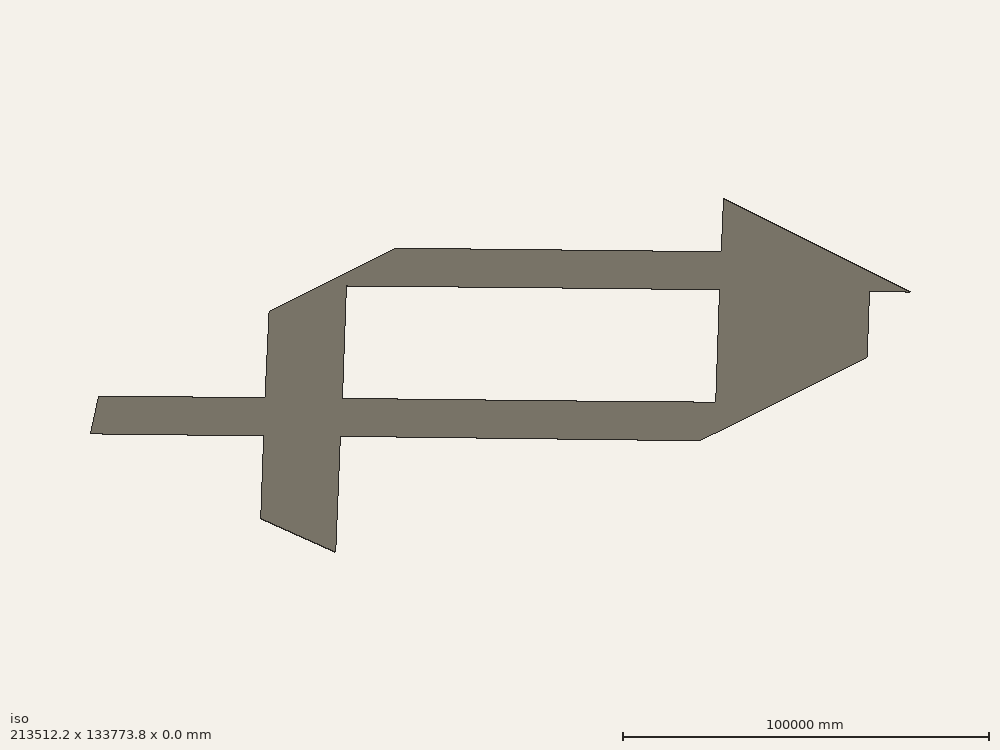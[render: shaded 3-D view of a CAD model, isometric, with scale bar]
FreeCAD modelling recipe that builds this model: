
FCSTD DOCUMENT  (FreeCAD 0.19R18652 (Git))
Label: 15 N_Hancock site
License: All rights reserved
LicenseURL: http://en.wikipedia.org/wiki/All_rights_reserved
objects: Part::Part2DObjectPython×68, App::FeaturePython×51, TechDraw::DrawViewSymbol×9, TechDraw::DrawViewDraft×8, TechDraw::DrawViewClip×5, App::DocumentObjectGroup×5, TechDraw::DrawSVGTemplate×4, TechDraw::DrawPage×4, Image::ImagePlane×1, Part::Cut×1
note: 69 computed .brp shape members not serialized (recipe doc carries the construction recipe); baked Part::Feature solids carry a one-line shape summary decoded from their .brp

FEATURE [Image::ImagePlane] ImagePlane
  XSize = 213448
  YSize = 133615
FEATURE [Part::Part2DObjectPython] Wire  # Draft 2D object (typed FeaturePython)
  Area = 1.04713e+09
  ChamferSize = 0
  Closed = true
  End = (3595.12,13281.7,0)
  FilletRadius = 0
  Length = 171081
  MakeFace = true
  Placement = pos=(-18425.3,-8041.37,0) rot=(0,0,1;0rad)
  Points = (8) [(0,0,0),(16501.4,-17298.5,0),(38495.4,4065.74,0),(31443.5,11545.3,0),(53741.5,33108.7,0),(46730.2,40390.5,0),(24402.7,18854.4,0),(22020.5,21323,0)]
  Start = (-18425.3,-8041.37,0)
  Subdivisions = 0
FEATURE [Part::Part2DObjectPython] Line  # Draft 2D object (typed FeaturePython)
  Area = 0
  ChamferSize = 0
  Closed = false
  End = (-26.9963,-49.3044,0)
  FilletRadius = 0
  Length = 57.0115
  MakeFace = true
  Placement = pos=(-66.3614,-8.06477,0) rot=(0,0,1;0rad)
  Points = (2) [(0,0,0),(39.3651,-41.2396,0)]
  Start = (-66.3614,-8.06477,0)
  Subdivisions = 0
FEATURE [Part::Part2DObjectPython] Wire001  label="Existing building"  # Draft 2D object (typed FeaturePython)
  Area = 4.1645e+08
  ChamferSize = 0
  Closed = true
  End = (802.63,10577.6,0)
  FilletRadius = 0
  Length = 81872.7
  MakeFace = true
  Placement = pos=(15936.7,-5214.36,0) rot=(0,0,1;0rad)
  Points = (4) [(0,0,0),(-13529.7,-13483.2,0),(-28601.5,2751.1,0),(-15134,15792,0)]
  Start = (15936.7,-5214.36,0)
  Subdivisions = 0
FEATURE [Part::Part2DObjectPython] Line001  # Draft 2D object (typed FeaturePython)
  Area = 0
  ChamferSize = 0
  Closed = false
  End = (-33624.1,7891.59,0)
  FilletRadius = 0
  Length = 61543.3
  MakeFace = true
  Placement = pos=(10791.9,50716.9,0) rot=(0,0,1;0rad)
  Points = (2) [(-112.189,-108.171,0),(-44415.9,-42825.3,0)]
  Start = (10679.7,50608.7,0)
  Subdivisions = 0
FEATURE [Part::Part2DObjectPython] Line002  # Draft 2D object (typed FeaturePython)
  Area = 0
  ChamferSize = 0
  Closed = false
  End = (3595.12,13281.7,0)
  FilletRadius = 0
  Length = 21954
  MakeFace = true
  Placement = pos=(3461.65,13054.6,0) rot=(0,0,1;0rad)
  Points = (2) [(-15002.8,16129,0),(133.473,227.049,0)]
  Start = (-11541.2,29183.7,0)
  Subdivisions = 0
FEATURE [Part::Part2DObjectPython] Line003  # Draft 2D object (typed FeaturePython)
  Area = 0
  ChamferSize = 0
  Closed = false
  End = (20070.1,-3975.63,0)
  FilletRadius = 0
  Length = 40805.7
  MakeFace = true
  Placement = pos=(20280.9,-3912.88,0) rot=(0,0,1;0rad)
  Points = (2) [(28041.8,-29505.8,0),(-210.816,-62.7537,0)]
  Start = (48322.6,-33418.7,0)
  Subdivisions = 0
FEATURE [Part::Part2DObjectPython] Line004  # Draft 2D object (typed FeaturePython)
  Area = 0
  ChamferSize = 0
  Closed = false
  End = (12819.8,-11272.6,0)
  FilletRadius = 0
  Length = 40597.7
  MakeFace = true
  Placement = pos=(12819.8,-11272.6,0) rot=(0,0,1;0rad)
  Points = (2) [(28094.1,-29306.8,0),(0,0,0)]
  Start = (40914,-40579.5,0)
  Subdivisions = 0
FEATURE [Part::Part2DObjectPython] Line005  # Draft 2D object (typed FeaturePython)
  Area = 0
  ChamferSize = 0
  Closed = false
  End = (9285.05,-36936.9,0)
  FilletRadius = 0
  Length = 20313.7
  MakeFace = true
  Placement = pos=(8396.39,-37813.2,0) rot=(0,0,1;0rad)
  Points = (2) [(15353.4,15138.7,0),(888.661,876.231,0)]
  Start = (23749.8,-22674.5,0)
  Subdivisions = 0
FEATURE [Part::Part2DObjectPython] Line006  # Draft 2D object (typed FeaturePython)
  Area = 0
  ChamferSize = 0
  Closed = false
  End = (56571.2,2831.99,0)
  FilletRadius = 0
  Length = 31050.5
  MakeFace = true
  Placement = pos=(57938.7,4146.14,0) rot=(0,0,1;0rad)
  Points = (2) [(-23756.1,-22829,0),(-1367.52,-1314.15,0)]
  Start = (34182.6,-18682.9,0)
  Subdivisions = 0
FEATURE [Part::Part2DObjectPython] Line007  # Draft 2D object (typed FeaturePython)
  Area = 0
  ChamferSize = 0
  Closed = false
  End = (49549.2,10177.8,0)
  FilletRadius = 0
  Length = 31069.9
  MakeFace = true
  Placement = pos=(50227.6,10829.7,0) rot=(0,0,1;0rad)
  Points = (2) [(-23080.2,-22180.9,0),(-678.339,-651.909,0)]
  Start = (27147.4,-11351.2,0)
  Subdivisions = 0
FEATURE [Part::Part2DObjectPython] Line008  # Draft 2D object (typed FeaturePython)
  Area = 0
  ChamferSize = 0
  Closed = false
  End = (20070.1,-3975.63,0)
  FilletRadius = 0
  Length = 31090.1
  MakeFace = true
  Placement = pos=(42737.8,18013.5,0) rot=(0,0,1;0rad)
  Points = (2) [(-352.194,-341.65,0),(-22667.8,-21989.1,0)]
  Start = (42385.6,17671.8,0)
  Subdivisions = 0
FEATURE [Part::Part2DObjectPython] Line009  # Draft 2D object (typed FeaturePython)
  Area = 0
  ChamferSize = 0
  Closed = false
  End = (-1096.7,18210.8,0)
  FilletRadius = 0
  Length = 30973.4
  MakeFace = true
  Placement = pos=(21701,40335.4,0) rot=(0,0,1;0rad)
  Points = (2) [(-570.551,-553.704,0),(-22797.7,-22124.6,0)]
  Start = (21130.5,39781.7,0)
  Subdivisions = 0
FEATURE [Part::Part2DObjectPython] Line010  # Draft 2D object (typed FeaturePython)
  Area = 0
  ChamferSize = 0
  Closed = false
  End = (-3426.03,20658,0)
  FilletRadius = 0
  Length = 30663.4
  MakeFace = true
  Placement = pos=(-2908.91,21158.5,0) rot=(0,0,1;0rad)
  Points = (2) [(-22551.3,-21825.2,0),(-517.124,-500.475,0)]
  Start = (-25460.2,-666.694,0)
  Subdivisions = 0
FEATURE [Part::Part2DObjectPython] Line011  # Draft 2D object (typed FeaturePython)
  Area = 0
  ChamferSize = 0
  Closed = false
  End = (-44317.6,19101.7,0)
  FilletRadius = 0
  Length = 37512.1
  MakeFace = true
  Placement = pos=(-18425.3,-8041.37,0) rot=(0,0,1;0rad)
  Points = (2) [(0,0,0),(-25892.3,27143.1,0)]
  Start = (-18425.3,-8041.37,0)
  Subdivisions = 0
FEATURE [Part::Part2DObjectPython] Line012  # Draft 2D object (typed FeaturePython)
  Area = 0
  ChamferSize = 0
  Closed = false
  End = (-103.235,61779.8,0)
  FilletRadius = 0
  Length = 40904.6
  MakeFace = true
  Placement = pos=(28304.8,32349.1,0) rot=(0,0,1;0rad)
  Points = (2) [(0,0,0),(-28408.1,29430.7,0)]
  Start = (28304.8,32349.1,0)
  Subdivisions = 0
FEATURE [Part::Part2DObjectPython] Line013  # Draft 2D object (typed FeaturePython)
  Area = 0
  ChamferSize = 0
  Closed = false
  End = (70621.3,-11866.1,0)
  FilletRadius = 0
  Length = 51093.3
  MakeFace = true
  Placement = pos=(35316.2,25067.3,0) rot=(0,0,1;0rad)
  Points = (2) [(0,0,0),(35305.1,-36933.5,0)]
  Start = (35316.2,25067.3,0)
  Subdivisions = 0
FEATURE [Part::Part2DObjectPython] Line014  # Draft 2D object (typed FeaturePython)
  Area = 0
  ChamferSize = 0
  Closed = false
  End = (26381.8,-54625.5,0)
  FilletRadius = 0
  Length = 40729.1
  MakeFace = true
  Placement = pos=(-1923.97,-25339.9,0) rot=(0,0,1;0rad)
  Points = (2) [(0,0,0),(28305.7,-29285.6,0)]
  Start = (-1923.97,-25339.9,0)
  Subdivisions = 0
FEATURE [Part::Part2DObjectPython] Line015  # Draft 2D object (typed FeaturePython)
  Area = 0
  ChamferSize = 0
  Closed = false
  End = (-44357.7,19063.1,0)
  FilletRadius = 0
  Length = 61507.5
  MakeFace = true
  Points = (2) [(-103.235,61779.8,0),(-44357.7,19063.1,0)]
  Start = (-103.235,61779.8,0)
  Subdivisions = 0
FEATURE [Part::Part2DObjectPython] Line016  # Draft 2D object (typed FeaturePython)
  Area = 0
  ChamferSize = 0
  Closed = false
  End = (26161.4,-54838.4,0)
  FilletRadius = 0
  Length = 61832.9
  MakeFace = true
  Points = (2) [(70621.3,-11866.1,0),(26161.4,-54838.4,0)]
  Start = (70621.3,-11866.1,0)
  Subdivisions = 0
FEATURE [Part::Part2DObjectPython] Wire002  # Draft 2D object (typed FeaturePython)
  Area = 0
  ChamferSize = 0
  Closed = false
  End = (8487.83,-66587.6,0)
  FilletRadius = 0
  Length = 162046
  MakeFace = true
  Placement = pos=(-105250,-39213.2,0) rot=(0,0,1;0rad)
  Points = (3) [(0,0,0),(45826.8,43996.5,0),(113738,-27374.4,0)]
  Start = (-105250,-39213.2,0)
  Subdivisions = 0
FEATURE [Part::Part2DObjectPython] Wire003  # Draft 2D object (typed FeaturePython)
  Area = 0
  ChamferSize = 0
  Closed = false
  End = (106683,-49683.6,0)
  FilletRadius = 0
  Length = 47347.4
  MakeFace = true
  Placement = pos=(72905.8,-66693,0) rot=(0,0,1;0rad)
  Points = (3) [(0,0,0),(25990.9,25090.7,0),(33776.8,17009.5,0)]
  Start = (72905.8,-66693,0)
  Subdivisions = 0
FEATURE [Part::Part2DObjectPython] Wire004  # Draft 2D object (typed FeaturePython)
  Area = 0
  ChamferSize = 0
  Closed = false
  End = (24054.2,66877.6,0)
  FilletRadius = 0
  Length = 118181
  MakeFace = true
  Placement = pos=(106665,22619.6,0) rot=(0,0,1;0rad)
  Points = (3) [(0,0,0),(-21005.7,-20112.4,0),(-82610.7,44257.9,0)]
  Start = (106665,22619.6,0)
  Subdivisions = 0
FEATURE [Part::Part2DObjectPython] Wire005  # Draft 2D object (typed FeaturePython)
  Area = 0
  ChamferSize = 0
  Closed = false
  End = (-90645.7,67080.7,0)
  FilletRadius = 0
  Length = 92567.1
  MakeFace = true
  Placement = pos=(-25016.6,66790,0) rot=(0,0,1;0rad)
  Points = (3) [(0,0,0),(-34041.5,-32480.4,0),(-65629,290.656,0)]
  Start = (-25016.6,66790,0)
  Subdivisions = 0
FEATURE [Part::Part2DObjectPython] Wire006  # Draft 2D object (typed FeaturePython)
  Area = 0
  ChamferSize = 0
  Closed = false
  End = (-106729,-11681.7,0)
  FilletRadius = 0
  Length = 92713.7
  MakeFace = true
  Placement = pos=(-106830,54078,0) rot=(0,0,1;0rad)
  Points = (3) [(0,0,0),(32714.7,-34282.2,0),(100.719,-65759.8,0)]
  Start = (-106830,54078,0)
  Subdivisions = 0
FEATURE [App::FeaturePython] Text  # WARN: FeaturePython — macro-defined, semantics opaque (R4)
  Placement = pos=(-45416.2,17806.4,0) rot=(0,0,-1;0.808978rad)
  Text = N HANCOCK ST
FEATURE [App::FeaturePython] Text001  # WARN: FeaturePython — macro-defined, semantics opaque (R4)
  Placement = pos=(-44903.8,19464,0) rot=(0,0,1;0.767719rad)
  Text = E MIFFLIN ST
FEATURE [App::FeaturePython] Text002  # WARN: FeaturePython — macro-defined, semantics opaque (R4)
  Placement = pos=(65660.9,-5269.52,0) rot=(0,0,-1;0.805821rad)
  Text = N FRANKLIN ST
FEATURE [App::FeaturePython] Text003  # WARN: FeaturePython — macro-defined, semantics opaque (R4)
  Placement = pos=(63903.1,-20917.1,0) rot=(0,0,1;0.768386rad)
  Text = E WASHINGTON AVE
FEATURE [Part::Part2DObjectPython] Line018  # Draft 2D object (typed FeaturePython)
  Area = 0
  ChamferSize = 0
  Closed = false
  End = (25014.2,29175,0)
  FilletRadius = 0
  Length = 10114.5
  MakeFace = true
  Points = (2) [(32029.6,21889,0),(25014.2,29175,0)]
  Start = (32029.6,21889,0)
  Subdivisions = 0
FEATURE [Part::Part2DObjectPython] Line022  # Draft 2D object (typed FeaturePython)
  Area = 0
  ChamferSize = 0
  Closed = false
  End = (1384.25,-22184.1,0)
  FilletRadius = 0
  Length = 23906.8
  MakeFace = true
  Points = (2) [(-15117.1,-4885.6,0),(1384.25,-22184.1,0)]
  Start = (-15117.1,-4885.6,0)
  Subdivisions = 0
FEATURE [App::FeaturePython] Dimension  # Draft dimension (typed FeaturePython)
  Diameter = false
  Dimline = (-1177.23,12550.3,0)
  Direction = (0,0,0)
  Distance = 30652.4
  End = (3595.12,13281.7,0)
  Normal = (0,0,1)
  Start = (-18425.3,-8041.37,0)
FEATURE [App::FeaturePython] Dimension001  # Draft dimension (typed FeaturePython)
  Diameter = false
  Dimline = (-7526.87,-23407.2,0)
  Direction = (0,0,0)
  Distance = 23906.8
  End = (-1923.97,-25339.9,0)
  Normal = (0,0,1)
  Start = (-18425.3,-8041.37,0)
FEATURE [App::FeaturePython] Dimension002  # Draft dimension (typed FeaturePython)
  Diameter = false
  Dimline = (19021.1,-8668.65,0)
  Direction = (0,0,0)
  Distance = 30662.2
  End = (20070.1,-3975.63,0)
  Normal = (0,0,1)
  Start = (-1923.97,-25339.9,0)
FEATURE [App::FeaturePython] Dimension003  # Draft dimension (typed FeaturePython)
  Diameter = false
  Dimline = (23033.4,28711.1,0)
  Direction = (0,0,0)
  Distance = 31021.3
  End = (28304.8,32349.1,0)
  Normal = (0,0,1)
  Start = (5977.33,10813,0)
FEATURE [App::FeaturePython] Dimension004  # Draft dimension (typed FeaturePython)
  Diameter = false
  Dimline = (36237.5,20611.2,0)
  Direction = (0,0,0)
  Distance = 31019
  End = (35316.2,25067.3,0)
  Normal = (0,0,1)
  Start = (13018.2,3503.93,0)
FEATURE [App::FeaturePython] Dimension005  # Draft dimension (typed FeaturePython)
  Diameter = false
  Dimline = (34894.1,26811.8,0)
  Direction = (0,0,0)
  Distance = 10108.5
  End = (35316.2,25067.3,0)
  Normal = (0,0,1)
  Start = (28304.8,32349.1,0)
FEATURE [App::FeaturePython] Dimension006  # Draft dimension (typed FeaturePython)
  Diameter = false
  Dimline = (-684.958,-23208.5,0)
  Direction = (0,0,0)
  Distance = 4572.19
  End = (1355.67,-22154.2,0)
  Normal = (0,0,1)
  Start = (-1923.97,-25339.9,0)
FEATURE [App::FeaturePython] Dimension007  # Draft dimension (typed FeaturePython)
  Diameter = false
  Dimline = (34178.3,24674.7,0)
  Direction = (0,0,0)
  Distance = 4572
  End = (35316.2,25067.3,0)
  Normal = (0,0,1)
  Start = (32022.7,21896.2,0)
FEATURE [Part::Part2DObjectPython] Line024  # Draft 2D object (typed FeaturePython)
  Area = 0
  ChamferSize = 0
  Closed = false
  End = (7804.54,5528.17,0)
  FilletRadius = 0
  Length = 40485.3
  MakeFace = true
  Placement = pos=(9504.84,7165.33,0) rot=(0,0,1;0rad)
  Points = (2) [(27463.5,26443.6,0),(-1700.31,-1637.16,0)]
  Start = (36968.4,33608.9,0)
  Subdivisions = 0
FEATURE [Part::Part2DObjectPython] Rectangle  # Draft 2D object (typed FeaturePython)
  Area = 1.50503e+07
  ChamferSize = 0
  Columns = 1
  FilletRadius = 0
  Height = 2743.2
  Length = 5486.4
  MakeFace = true
  Placement = pos=(22172.4,23739,0) rot=(0,0,-1;0.018041rad)
  Rows = 1
FEATURE [Part::Part2DObjectPython] Rectangle001  label="Rectangle"  # Draft 2D object (typed FeaturePython)
  Area = 1.50503e+07
  ChamferSize = 0
  Columns = 1
  FilletRadius = 0
  Height = 2743.2
  Length = 5486.4
  MakeFace = true
  Placement = pos=(19380.2,21045.8,0) rot=(0,0,-1;0.018041rad)
  Rows = 1
FEATURE [Part::Part2DObjectPython] Rectangle002  label="Rectangle"  # Draft 2D object (typed FeaturePython)
  Area = 1.50503e+07
  ChamferSize = 0
  Columns = 1
  FilletRadius = 0
  Height = 2743.2
  Length = 5486.4
  MakeFace = true
  Placement = pos=(16587.9,18352.5,0) rot=(0,0,-1;0.018041rad)
  Rows = 1
FEATURE [Part::Part2DObjectPython] Rectangle003  label="Rectangle"  # Draft 2D object (typed FeaturePython)
  Area = 1.50503e+07
  ChamferSize = 0
  Columns = 1
  FilletRadius = 0
  Height = 2743.2
  Length = 5486.4
  MakeFace = true
  Placement = pos=(11003.5,12966,0) rot=(0,0,-1;0.018041rad)
  Rows = 1
FEATURE [Part::Part2DObjectPython] Rectangle004  label="Rectangle"  # Draft 2D object (typed FeaturePython)
  Area = 1.50503e+07
  ChamferSize = 0
  Columns = 1
  FilletRadius = 0
  Height = 2743.2
  Length = 5486.4
  MakeFace = true
  Placement = pos=(13795.7,15659.2,0) rot=(0,0,-1;0.018041rad)
  Rows = 1
FEATURE [Part::Part2DObjectPython] Rectangle005  label="Rectangle"  # Draft 2D object (typed FeaturePython)
  Area = 1.50503e+07
  ChamferSize = 0
  Columns = 1
  FilletRadius = 0
  Height = 2743.2
  Length = 5486.4
  MakeFace = true
  Placement = pos=(8211.22,10272.7,0) rot=(0,0,-1;0.018041rad)
  Rows = 1
FEATURE [Part::Part2DObjectPython] Rectangle007  label="Rectangle"  # Draft 2D object (typed FeaturePython)
  Area = 1.50503e+07
  ChamferSize = 0
  Columns = 1
  FilletRadius = 0
  Height = 2743.2
  Length = 5486.4
  MakeFace = true
  Placement = pos=(23038.1,27272.4,0) rot=(0,0,-1;0.804317rad)
  Rows = 1
FEATURE [App::FeaturePython] Text004  # WARN: FeaturePython — macro-defined, semantics opaque (R4)
  Placement = pos=(-16015.3,-6054.01,0) rot=(0,0,-1;0.808978rad)
  Text = SETBACK
FEATURE [App::FeaturePython] Text005  # WARN: FeaturePython — macro-defined, semantics opaque (R4)
  Placement = pos=(25183.8,29191.7,0) rot=(0,0,-1;0.808978rad)
  Text = SETBACK
FEATURE [App::FeaturePython] Text006  # WARN: FeaturePython — macro-defined, semantics opaque (R4)
  Placement = pos=(36344.8,32541.2,0) rot=(0,0,-1;0.807936rad)
  Text = ONLY 50% OF THE FRONTAGE | CAN BE OCCUPIED BY | PARKING
FEATURE [App::FeaturePython] Dimension009  # Draft dimension (typed FeaturePython)
  Diameter = false
  Dimline = (27213.5,18597.6,0)
  Direction = (0,0,0)
  Distance = 4302.77
  End = (27856.8,17853.7,0)
  Normal = (0,0,1)
  Start = (24865.7,20946.8,0)
FEATURE [Part::Part2DObjectPython] Line025  # Draft 2D object (typed FeaturePython)
  Area = 0
  ChamferSize = 0
  Closed = false
  End = (21204.7,17415.6,0)
  FilletRadius = 0
  Length = 7995.18
  MakeFace = true
  Placement = pos=(27657.9,23640,0) rot=(0,0,1;0rad)
  Points = (2) [(-698.692,-673.925,0),(-6453.21,-6224.46,0)]
  Start = (26959.2,22966.1,0)
  Subdivisions = 0
FEATURE [App::FeaturePython] Dimension008  # Draft dimension (typed FeaturePython)
  Diameter = false
  Dimline = (28275.6,26130.3,0)
  Direction = (0,0,0)
  Distance = 5097.53
  End = (28549.8,25503,0)
  Normal = (0,0,1)
  Start = (25014.2,29175,0)
FEATURE [Part::Part2DObjectPython] Circle  # Draft 2D object (typed FeaturePython)
  Area = 1.11035e+07
  FirstAngle = 0
  LastAngle = 0
  MakeFace = true
  Placement = pos=(-45678.7,-16653.5,0) rot=(0,0,1;0rad)
  Radius = 1879.98
FEATURE [Part::Part2DObjectPython] Line027  # Draft 2D object (typed FeaturePython)
  Area = 0
  ChamferSize = 0
  Closed = false
  End = (-45678.7,-18533.5,0)
  FilletRadius = 0
  Length = 3759.97
  MakeFace = true
  Placement = pos=(-45678.7,-14773.5,0) rot=(0,0,1;0rad)
  Points = (2) [(0,0,0),(0,-3759.97,0)]
  Start = (-45678.7,-14773.5,0)
  Subdivisions = 0
FEATURE [Part::Part2DObjectPython] Wire007  # Draft 2D object (typed FeaturePython)
  Area = 3.53434e+06
  ChamferSize = 0
  Closed = true
  End = (-43798.7,-16653.5,0)
  FilletRadius = 0
  Length = 9077.37
  MakeFace = true
  Placement = pos=(-47558.7,-16653.5,0) rot=(0,0,1;0rad)
  Points = (3) [(0,0,0),(1879.98,1879.98,0),(3759.97,0,0)]
  Start = (-47558.7,-16653.5,0)
  Subdivisions = 0
FEATURE [Part::Part2DObjectPython] Wire008  label="Sta norte"  # Draft 2D object (typed FeaturePython)
  Area = 1.76717e+06
  ChamferSize = 0
  Closed = true
  End = (-45678.7,-16653.5,0)
  FilletRadius = 0
  Length = 6418.67
  MakeFace = true
  Placement = pos=(-47558.7,-16653.5,0) rot=(0,0,1;0rad)
  Points = (3) [(0,0,0),(1879.98,1879.98,0),(1879.98,0,0)]
  Start = (-47558.7,-16653.5,0)
  Subdivisions = 0
FEATURE [App::FeaturePython] Text007  # WARN: FeaturePython — macro-defined, semantics opaque (R4)
  Placement = pos=(-2690.19,-1131.57,0) rot=(0,0,-1;0.808978rad)
  Text = EXISTING BUILDING
FEATURE [App::FeaturePython] Text008  # WARN: FeaturePython — macro-defined, semantics opaque (R4)
  Placement = pos=(19057.9,12203.9,0) rot=(0,0,1;0.763757rad)
  Text = 6 x 9x18 STALLS
FEATURE [Part::Part2DObjectPython] Wire009  # Draft 2D object (typed FeaturePython)
  Area = 6.39951e+08
  ChamferSize = 0
  Closed = true
  End = (-1923.97,-25339.9,0)
  FilletRadius = 0
  Length = 101357
  MakeFace = true
  Placement = pos=(-18425.3,-8041.37,0) rot=(0,0,1;0rad)
  Points = (5) [(0,0,0),(19228,18619,0),(34362,2827,0),(35739.9,1389.18,0),(16501.4,-17298.5,0)]
  Start = (-18425.3,-8041.37,0)
  Subdivisions = 0
FEATURE [Part::Part2DObjectPython] Wire010  label="Blue cotour"  # Draft 2D object (typed FeaturePython)
  Area = 2.09786e+08
  ChamferSize = 0
  Closed = true
  End = (24964.7,26432.3,0)
  FilletRadius = 0
  Length = 78881.9
  MakeFace = true
  Placement = pos=(27702.6,26382.9,0) rot=(0,0,1;0rad)
  Points = (24) [(0,0,0),(1728.63,-31.1927,0),(4134.48,2285.31,0),(6554.12,-220.027,0),(3269.91,-3396.04,0),(4326.97,-4493.86,0),(-7977.16,-16317.9,0),+17 more]
  Start = (27702.6,26382.9,0)
  Subdivisions = 0
FEATURE [Part::Part2DObjectPython] Wire011  # Draft 2D object (typed FeaturePython)
  Area = 1.87779e+08
  ChamferSize = 0
  Closed = true
  End = (-1923.97,-25339.9,0)
  FilletRadius = 0
  Length = 63520
  MakeFace = true
  Placement = pos=(-18425.3,-8041.37,0) rot=(1,0,0;3.14159rad)
  Points = (4) [(0,0,0),(5760.55,-5578.1,0),(22021.1,11936.8,0),(16501.4,17298.5,0)]
  Start = (-18425.3,-8041.37,0)
  Subdivisions = 0
FEATURE [Part::Part2DObjectPython] Wire012  # Draft 2D object (typed FeaturePython)
  Area = 1.7888e+10
  ChamferSize = 0
  Closed = true
  End = (-74114.9,19795.9,0)
  FilletRadius = 0
  Length = 746954
  MakeFace = true
  Placement = pos=(-106830,54078,0) rot=(0,0,1;0rad)
  Points = (15) [(0,0,0),(16183.9,13002.7,0),(47762.3,-19758.9,0),(81812.9,12712,0),(130884,12799.5,0),(192489,-51570.8,0),(213495,-31458.4,0),(213512,-103762,0),+7 more]
  Start = (-106830,54078,0)
  Subdivisions = 0
FEATURE [Part::Part2DObjectPython] Wire013  # Draft 2D object (typed FeaturePython)
  Area = 6.29559e+09
  ChamferSize = 0
  Closed = true
  End = (-1923.97,-25339.9,0)
  FilletRadius = 0
  Length = 327288
  MakeFace = true
  Placement = pos=(-44357.7,19063.1,0) rot=(0,0,1;0rad)
  Points = (6) [(0,0,0),(44254.4,42716.7,0),(79673.8,6004.29,0),(114979,-30929.2,0),(70739.4,-73688.5,0),(42433.7,-44402.9,0)]
  Start = (-44357.7,19063.1,0)
  Subdivisions = 0
FEATURE [Part::Cut] Cut
  Base = -> Wire012
  Tool = -> Wire013
FEATURE [TechDraw::DrawSVGTemplate] Template
  EditableTexts = ADDRESS=15N HANCOCK ST, MADISON WI; DATE=Date; DESCRIPTION=Description; PROJECT NAME=STUDY FOR A BACKLOT
  Height = 279.4
  Orientation = 1
  Width = 431.8
FEATURE [TechDraw::DrawViewSymbol] Symbol
  EditableTexts = 01 | PLAN VIEW OF PARCEL | 1/32 = 1-0
  LockPosition = false
  Rotation = 0
  ScaleType = 2
  Symbol = <blob: 4965 chars omitted>
  X = 87.9124
  Y = 44.9176
FEATURE [TechDraw::DrawViewSymbol] Symbol001
  LockPosition = false
  Rotation = 0
  Scale = 0.35
  ScaleType = 2
  Symbol = <blob: 2355908 chars omitted>
  X = -0.52207
  Y = 0.671524
FEATURE [TechDraw::DrawViewClip] Clip001
  Height = 60.96
  LockPosition = false
  Rotation = 0
  ScaleType = 0
  ShowFrame = false
  Views = -> [Symbol001]
  Width = 60.96
  X = 60.1906
  Y = 100.238
FEATURE [App::DocumentObjectGroup] Group001  label="Existing"
  Group = -> [Wire001,Wire011,Cut,Wire,Line,Line001,Line002,Line003,Line004,Line005,Line006,Line007,Line008,Line009,Line010,Line011,Line012,Line013,Line014,Line015,Line016,Wire002,Wire003,Wire004,Wire006,Wire005,Line022,Line018,Wire009,Wire008,Wire007,Line027,Circle,Text007,Text005,Dimension007,Dimension005,Dimension006,Dimension004,Dimension003,Dimension002,Dimension001,Dimension,Text003,Text002,Text001,Text]
FEATURE [TechDraw::DrawViewDraft] DraftView
  Direction = (0,0,1)
  FontSize = 5.5
  LineSpacing = 5
  LineStyle = Solid
  LineWidth = 0.15
  LockPosition = false
  OverrideStyle = false
  Rotation = 0
  Scale = 0.00260417
  ScaleType = 2
  Source = -> Group001
  Symbol = <blob: 16925 chars omitted>
  X = 0
  Y = 0
FEATURE [App::DocumentObjectGroup] Group002  label="Parking only"
  Group = -> [Wire010,Line024,Rectangle,Rectangle001,Rectangle002,Rectangle003,Rectangle004,Rectangle005,Rectangle007,Line025,Dimension008,Text004,Text006,Dimension009,Text008]
FEATURE [Part::Part2DObjectPython] Line029  # Draft 2D object (typed FeaturePython)
  Area = 0
  ChamferSize = 0
  Closed = false
  End = (25711.8,28450.5,0)
  FilletRadius = 0
  Length = 20353.1
  MakeFace = true
  Points = (2) [(11062.7,14320.7,0),(25711.8,28450.5,0)]
  Start = (11062.7,14320.7,0)
  Subdivisions = 0
FEATURE [Part::Part2DObjectPython] Line032  # Draft 2D object (typed FeaturePython)
  Area = 0
  ChamferSize = 0
  Closed = false
  End = (35316.2,25067.3,0)
  FilletRadius = 0
  Length = 31019
  MakeFace = true
  Placement = pos=(13018.2,3503.93,0) rot=(0,0,1;0rad)
  Points = (2) [(0,0,0),(22298,21563.4,0)]
  Start = (13018.2,3503.93,0)
  Subdivisions = 0
FEATURE [Part::Part2DObjectPython] Line033  # Draft 2D object (typed FeaturePython)
  Area = 0
  ChamferSize = 0
  Closed = false
  End = (31331.9,22613.6,0)
  FilletRadius = 0
  Length = 20351.2
  MakeFace = true
  Points = (2) [(16702.5,8466.08,0),(31331.9,22613.6,0)]
  Start = (16702.5,8466.08,0)
  Subdivisions = 0
FEATURE [Part::Part2DObjectPython] Line036  # Draft 2D object (typed FeaturePython)
  Area = 0
  ChamferSize = 0
  Closed = false
  End = (13018.2,3503.93,0)
  FilletRadius = 0
  Length = 10148.7
  MakeFace = true
  Placement = pos=(5977.33,10813,0) rot=(0,0,1;0rad)
  Points = (2) [(0,0,0),(7040.85,-7309.08,0)]
  Start = (5977.33,10813,0)
  Subdivisions = 0
FEATURE [App::FeaturePython] Dimension010  # Draft dimension (typed FeaturePython)
  Diameter = false
  Dimline = (23300,27000,0)
  Direction = (0,0,0)
  Distance = 1005.84
  End = (25711.8,28450.5,0)
  Normal = (0,0,1)
  Start = (25014.2,29175,0)
FEATURE [App::FeaturePython] Dimension011  # Draft dimension (typed FeaturePython)
  Diameter = false
  Dimline = (23735.6,26547.6,0)
  Direction = (0,0,0)
  Distance = 1005.84
  End = (32031.2,21890.5,0)
  Normal = (0,0,1)
  Start = (31331.9,22613.6,0)
FEATURE [Part::Part2DObjectPython] Line037  # Draft 2D object (typed FeaturePython)
  Area = 0
  ChamferSize = 0
  Closed = false
  End = (17408.5,7733.14,0)
  FilletRadius = 0
  Length = 10148.7
  MakeFace = true
  Points = (2) [(10367.7,15042.2,0),(17408.5,7733.14,0)]
  Start = (10367.7,15042.2,0)
  Subdivisions = 0
FEATURE [App::FeaturePython] Dimension012  # Draft dimension (typed FeaturePython)
  Diameter = false
  Dimline = (17400.3,7741.68,0)
  Direction = (0,0,0)
  Distance = 6096.01
  End = (17400.3,7741.68,0)
  Normal = (0,0,1)
  Start = (13018.2,3503.93,0)
FEATURE [App::FeaturePython] Text010  # WARN: FeaturePython — macro-defined, semantics opaque (R4)
  Placement = pos=(7530.44,6471.84,0) rot=(0,0,-1;0.801487rad)
  Text = OPEN SPACE
FEATURE [App::FeaturePython] Text011  # WARN: FeaturePython — macro-defined, semantics opaque (R4)
  Placement = pos=(9130.44,11571.8,0) rot=(0,0,-1;0.801487rad)
  Text = OPEN SPACE
FEATURE [App::FeaturePython] Dimension013  # Draft dimension (typed FeaturePython)
  Diameter = false
  Dimline = (20070.1,-3975.63,0)
  Direction = (0,0,0)
  Distance = 3841.42
  End = (20070.1,-3975.63,0)
  Normal = (0,0,1)
  Start = (17314.6,-6652.19,0)
FEATURE [Part::Part2DObjectPython] Line038  # Draft 2D object (typed FeaturePython)
  Area = 0
  ChamferSize = 0
  Closed = false
  End = (28077.4,18083.6,0)
  FilletRadius = 0
  Length = 8217.7
  MakeFace = true
  Points = (2) [(22377.6,24003.3,0),(28077.4,18083.6,0)]
  Start = (22377.6,24003.3,0)
  Subdivisions = 0
FEATURE [Part::Part2DObjectPython] Line042  # Draft 2D object (typed FeaturePython)
  Area = 0
  ChamferSize = 0
  Closed = false
  End = (26183,20051.1,0)
  FilletRadius = 0
  Length = 5486.41
  MakeFace = true
  Points = (2) [(30126.9,23865.1,0),(26183,20051.1,0)]
  Start = (30126.9,23865.1,0)
  Subdivisions = 0
FEATURE [Part::Part2DObjectPython] Line043  # Draft 2D object (typed FeaturePython)
  Area = 0
  ChamferSize = 0
  Closed = false
  End = (24280.3,22027.2,0)
  FilletRadius = 0
  Length = 5486.41
  MakeFace = true
  Points = (2) [(28224.2,25841.2,0),(24280.3,22027.2,0)]
  Start = (28224.2,25841.2,0)
  Subdivisions = 0
FEATURE [Part::Part2DObjectPython] Line044  # Draft 2D object (typed FeaturePython)
  Area = 0
  ChamferSize = 0
  Closed = false
  End = (26321.5,27817.3,0)
  FilletRadius = 0
  Length = 5486.41
  MakeFace = true
  Points = (2) [(22377.6,24003.3,0),(26321.5,27817.3,0)]
  Start = (22377.6,24003.3,0)
  Subdivisions = 0
FEATURE [Part::Part2DObjectPython] Line045  # Draft 2D object (typed FeaturePython)
  Area = 0
  ChamferSize = 0
  Closed = false
  End = (32029.6,21889,0)
  FilletRadius = 0
  Length = 8229.62
  MakeFace = true
  Placement = pos=(26321.5,27817.3,0) rot=(0,0,1;0rad)
  Points = (2) [(0,0,0),(5708.09,-5928.26,0)]
  Start = (26321.5,27817.3,0)
  Subdivisions = 0
FEATURE [Part::Part2DObjectPython] Wire014  label="Building contour"  # Draft 2D object (typed FeaturePython)
  Area = 1.20638e+08
  ChamferSize = 0
  Closed = true
  End = (21763,24641.6,0)
  FilletRadius = 0
  Length = 45954.7
  MakeFace = true
  Placement = pos=(11062.7,14320.7,0) rot=(0,0,1;0rad)
  Points = (4) [(0,0,0),(5651.09,-5843.6,0),(16325.3,4478.95,0),(10700.3,10321,0)]
  Start = (11062.7,14320.7,0)
  Subdivisions = 0
FEATURE [App::FeaturePython] Text012  # WARN: FeaturePython — macro-defined, semantics opaque (R4)
  Placement = pos=(16915.7,18408.6,0) rot=(0,0,-1;0rad)
  Text = NEW | BUILDING | 1300.70 SQFT
FEATURE [App::FeaturePython] Dimension014  # Draft dimension (typed FeaturePython)
  Diameter = false
  Dimline = (16000,9600,0)
  Direction = (0,0,0)
  Distance = 8129.12
  End = (16713.8,8477.07,0)
  Normal = (0,0,1)
  Start = (11062.7,14320.7,0)
FEATURE [App::FeaturePython] Dimension015  # Draft dimension (typed FeaturePython)
  Diameter = false
  Dimline = (26800,18600,0)
  Direction = (0,0,0)
  Distance = 14864.8
  End = (27388,18799.6,0)
  Normal = (0,0,1)
  Start = (16702.5,8466.08,0)
FEATURE [App::FeaturePython] Text013  # WARN: FeaturePython — macro-defined, semantics opaque (R4)
  Placement = pos=(26502.5,23589.1,0) rot=(0,0,-1;0.000587rad)
  Text = 3 x 9x18' | STALLS
FEATURE [TechDraw::DrawViewDraft] DraftView001
  Direction = (0,0,1)
  FontSize = 5.5
  LineSpacing = 5
  LineStyle = Solid
  LineWidth = 0.15
  LockPosition = false
  OverrideStyle = false
  Rotation = 0
  Scale = 0.00260417
  ScaleType = 2
  Source = -> Group002
  Symbol = <blob: 7460 chars omitted>
  X = 274.42
  Y = 206.151
FEATURE [TechDraw::DrawViewClip] Clip002
  Height = 213.36
  LockPosition = false
  Rotation = 0
  ScaleType = 0
  ShowFrame = false
  Views = -> [DraftView]
  Width = 396.24
  X = 215.9
  Y = 155.7
FEATURE [TechDraw::DrawSVGTemplate] Template001
  EditableTexts = ADDRESS=15N HANCOCK ST, MADISON WI; PROJECT NAME=STUDY FOR A BACKLOT
  Height = 279.4
  Orientation = 1
  Width = 431.8
FEATURE [TechDraw::DrawViewSymbol] Symbol002
  EditableTexts = 01 | PLAN VIEW OF PARCEL - SPLIT LOT W/ PARKING | 1/32 = 1-0
  LockPosition = false
  Rotation = 0
  ScaleType = 2
  Symbol = <blob: 4988 chars omitted>
  X = 87.9124
  Y = 44.9176
FEATURE [TechDraw::DrawViewDraft] DraftView003
  Direction = (0,0,1)
  FontSize = 5.5
  LineSpacing = 5
  LineStyle = Solid
  LineWidth = 0.15
  LockPosition = false
  OverrideStyle = false
  Rotation = 0
  Scale = 0.00260417
  ScaleType = 2
  Source = -> Group001
  Symbol = <blob: 16925 chars omitted>
  X = -20.9742
  Y = -2.70531
FEATURE [TechDraw::DrawViewClip] Clip
  Height = 213.36
  LockPosition = false
  Rotation = 0
  ScaleType = 0
  ShowFrame = false
  Views = -> [DraftView003]
  Width = 396.24
  X = 215.9
  Y = 155.7
FEATURE [App::FeaturePython] Text014  # WARN: FeaturePython — macro-defined, semantics opaque (R4)
  Placement = pos=(19615.7,20408.6,0) rot=(0,0,-1;0.016745rad)
  Text = NEW | BUILDING | 2714.21 SQFT
FEATURE [Part::Part2DObjectPython] Line046  # Draft 2D object (typed FeaturePython)
  Area = 0
  ChamferSize = 0
  Closed = false
  End = (13018.2,3503.93,0)
  FilletRadius = 0
  Length = 10148.7
  MakeFace = true
  Placement = pos=(5977.33,10813,0) rot=(0,0,1;0rad)
  Points = (2) [(0,0,0),(7040.85,-7309.08,0)]
  Start = (5977.33,10813,0)
  Subdivisions = 0
FEATURE [Part::Part2DObjectPython] Line047  # Draft 2D object (typed FeaturePython)
  Area = 0
  ChamferSize = 0
  Closed = false
  End = (31331.9,22613.6,0)
  FilletRadius = 0
  Length = 20351.2
  MakeFace = true
  Points = (2) [(16702.5,8466.08,0),(31331.9,22613.6,0)]
  Start = (16702.5,8466.08,0)
  Subdivisions = 0
FEATURE [App::FeaturePython] Dimension016  # Draft dimension (typed FeaturePython)
  Diameter = false
  Dimline = (23735.6,26547.6,0)
  Direction = (0,0,0)
  Distance = 1005.84
  End = (32031.2,21890.5,0)
  Normal = (0,0,1)
  Start = (31331.9,22613.6,0)
FEATURE [Part::Part2DObjectPython] Line050  # Draft 2D object (typed FeaturePython)
  Area = 0
  ChamferSize = 0
  Closed = false
  End = (17408.5,7733.14,0)
  FilletRadius = 0
  Length = 10148.7
  MakeFace = true
  Points = (2) [(10367.7,15042.2,0),(17408.5,7733.14,0)]
  Start = (10367.7,15042.2,0)
  Subdivisions = 0
FEATURE [App::FeaturePython] Dimension017  # Draft dimension (typed FeaturePython)
  Diameter = false
  Dimline = (17400.3,7741.68,0)
  Direction = (0,0,0)
  Distance = 6096.01
  End = (17400.3,7741.68,0)
  Normal = (0,0,1)
  Start = (13018.2,3503.93,0)
FEATURE [App::FeaturePython] Text015  # WARN: FeaturePython — macro-defined, semantics opaque (R4)
  Placement = pos=(7130.44,6971.84,0) rot=(0,0,-1;0.801487rad)
  Text = OPEN SPACE
FEATURE [App::FeaturePython] Dimension018  # Draft dimension (typed FeaturePython)
  Diameter = false
  Dimline = (23300,27000,0)
  Direction = (0,0,0)
  Distance = 1005.84
  End = (25711.8,28450.5,0)
  Normal = (0,0,1)
  Start = (25014.2,29175,0)
FEATURE [Part::Part2DObjectPython] Line051  # Draft 2D object (typed FeaturePython)
  Area = 0
  ChamferSize = 0
  Closed = false
  End = (25711.8,28450.5,0)
  FilletRadius = 0
  Length = 20353.1
  MakeFace = true
  Points = (2) [(11062.7,14320.7,0),(25711.8,28450.5,0)]
  Start = (11062.7,14320.7,0)
  Subdivisions = 0
FEATURE [Part::Part2DObjectPython] Line052  # Draft 2D object (typed FeaturePython)
  Area = 0
  ChamferSize = 0
  Closed = false
  End = (35316.2,25067.3,0)
  FilletRadius = 0
  Length = 31019
  MakeFace = true
  Placement = pos=(13018.2,3503.93,0) rot=(0,0,1;0rad)
  Points = (2) [(0,0,0),(22298,21563.4,0)]
  Start = (13018.2,3503.93,0)
  Subdivisions = 0
FEATURE [App::FeaturePython] Text016  # WARN: FeaturePython — macro-defined, semantics opaque (R4)
  Placement = pos=(9130.44,11571.8,0) rot=(0,0,-1;0.801487rad)
  Text = OPEN SPACE
FEATURE [App::FeaturePython] Dimension019  # Draft dimension (typed FeaturePython)
  Diameter = false
  Dimline = (20070.1,-3975.63,0)
  Direction = (0,0,0)
  Distance = 3841.42
  End = (20070.1,-3975.63,0)
  Normal = (0,0,1)
  Start = (17314.6,-6652.19,0)
FEATURE [Part::Part2DObjectPython] Wire015  label="Building Contour"  # Draft 2D object (typed FeaturePython)
  Area = 1.65185e+08
  ChamferSize = 0
  Closed = true
  End = (25711.8,28450.5,0)
  FilletRadius = 0
  Length = 56927.5
  MakeFace = true
  Placement = pos=(11062.7,14320.7,0) rot=(0,0,1;0rad)
  Points = (4) [(0,0,0),(5651.09,-5843.6,0),(20274.1,8287.8,0),(14649.1,14129.8,0)]
  Start = (11062.7,14320.7,0)
  Subdivisions = 0
FEATURE [App::FeaturePython] Dimension020  # Draft dimension (typed FeaturePython)
  Diameter = false
  Dimline = (16000,9600,0)
  Direction = (0,0,0)
  Distance = 8129.12
  End = (16713.8,8477.07,0)
  Normal = (0,0,1)
  Start = (11062.7,14320.7,0)
FEATURE [App::FeaturePython] Dimension021  # Draft dimension (typed FeaturePython)
  Diameter = false
  Dimline = (26800,18600,0)
  Direction = (0,0,0)
  Distance = 20351.2
  End = (31331.9,22613.6,0)
  Normal = (0,0,1)
  Start = (16702.5,8466.08,0)
FEATURE [TechDraw::DrawViewSymbol] Symbol003
  EditableTexts = 01 | PLAN VIEW OF PARCEL  -SPLIT LOT | 1/32 = 1-0
  LockPosition = false
  Rotation = 0
  ScaleType = 2
  Symbol = <blob: 4977 chars omitted>
  X = 87.9124
  Y = 44.9176
FEATURE [TechDraw::DrawSVGTemplate] Template002
  EditableTexts = ADDRESS=15N HANCOCK ST, MADISON WI; PROJECT NAME=STUDY FOR A BACKLOT
  Height = 279.4
  Orientation = 1
  Width = 431.8
FEATURE [TechDraw::DrawViewDraft] DraftView005
  Direction = (0,0,1)
  FontSize = 5.5
  LineSpacing = 5
  LineStyle = Solid
  LineWidth = 0.15
  LockPosition = false
  OverrideStyle = false
  Rotation = 0
  Scale = 0.00260417
  ScaleType = 2
  Source = -> Group001
  Symbol = <blob: 16925 chars omitted>
  X = -33.1876
  Y = 4.23342
FEATURE [TechDraw::DrawViewClip] Clip003
  Height = 213.36
  LockPosition = false
  Rotation = 0
  ScaleType = 0
  ShowFrame = false
  Views = -> [DraftView005]
  Width = 396.24
  X = 215.9
  Y = 155.7
FEATURE [App::FeaturePython] Dimension022  # Draft dimension (typed FeaturePython)
  Diameter = false
  Dimline = (23300,27000,0)
  Direction = (0,0,0)
  Distance = 1005.84
  End = (25711.8,28450.5,0)
  Normal = (0,0,1)
  Start = (25014.2,29175,0)
FEATURE [App::FeaturePython] Text017  # WARN: FeaturePython — macro-defined, semantics opaque (R4)
  Placement = pos=(11109.3,13506.3,0) rot=(0,0,-1;0.801487rad)
  Text = OPEN SPACE
FEATURE [Part::Part2DObjectPython] Line054  # Draft 2D object (typed FeaturePython)
  Area = 0
  ChamferSize = 0
  Closed = false
  End = (25711.8,28450.5,0)
  FilletRadius = 0
  Length = 12062.5
  MakeFace = true
  Points = (2) [(17029.8,20076.3,0),(25711.8,28450.5,0)]
  Start = (17029.8,20076.3,0)
  Subdivisions = 0
FEATURE [App::FeaturePython] Text019  # WARN: FeaturePython — macro-defined, semantics opaque (R4)
  Placement = pos=(21515.7,22908.6,0) rot=(0,0,-1;0.016745rad)
  Text = NEW | BUILDING | 1057.20 SQFT
FEATURE [Part::Part2DObjectPython] Line055  # Draft 2D object (typed FeaturePython)
  Area = 0
  ChamferSize = 0
  Closed = false
  End = (31331.9,22613.6,0)
  FilletRadius = 0
  Length = 12081.6
  MakeFace = true
  Points = (2) [(22647.1,14214.8,0),(31331.9,22613.6,0)]
  Start = (22647.1,14214.8,0)
  Subdivisions = 0
FEATURE [App::FeaturePython] Dimension025  # Draft dimension (typed FeaturePython)
  Diameter = false
  Dimline = (23735.6,26547.6,0)
  Direction = (0,0,0)
  Distance = 1005.84
  End = (32031.2,21890.5,0)
  Normal = (0,0,1)
  Start = (31331.9,22613.6,0)
FEATURE [App::FeaturePython] Dimension027  # Draft dimension (typed FeaturePython)
  Diameter = false
  Dimline = (26800,18600,0)
  Direction = (0,0,0)
  Distance = 12081.6
  End = (31331.9,22613.6,0)
  Normal = (0,0,1)
  Start = (22647.1,14214.8,0)
FEATURE [App::FeaturePython] Dimension026  # Draft dimension (typed FeaturePython)
  Diameter = false
  Dimline = (16000,9600,0)
  Direction = (0,0,0)
  Distance = 8129.12
  End = (16713.8,8477.07,0)
  Normal = (0,0,1)
  Start = (11062.7,14320.7,0)
FEATURE [Part::Part2DObjectPython] Line057  # Draft 2D object (typed FeaturePython)
  Area = 0
  ChamferSize = 0
  Closed = false
  End = (16333.9,20802.5,0)
  FilletRadius = 0
  Length = 10130.2
  MakeFace = true
  Points = (2) [(23343,13488.6,0),(16333.9,20802.5,0)]
  Start = (23343,13488.6,0)
  Subdivisions = 0
FEATURE [App::FeaturePython] Dimension028  # Draft dimension (typed FeaturePython)
  Diameter = false
  Dimline = (20600,12200,0)
  Direction = (0,0,0)
  Distance = 18288
  End = (21573.3,15335.2,0)
  Normal = (0,0,1)
  Start = (8369.65,2681.63,0)
FEATURE [Part::Part2DObjectPython] Wire016  label="Building Contour"  # Draft 2D object (typed FeaturePython)
  Area = 9.79116e+07
  ChamferSize = 0
  Closed = true
  End = (22647.1,14214.8,0)
  FilletRadius = 0
  Length = 40365.4
  MakeFace = true
  Placement = pos=(17029.8,20076.3,0) rot=(0,0,1;0rad)
  Points = (4) [(0,0,0),(8681.98,8374.23,0),(14302.1,2537.34,0),(5617.22,-5861.42,0)]
  Start = (17029.8,20076.3,0)
  Subdivisions = 0
FEATURE [TechDraw::DrawSVGTemplate] Template003
  EditableTexts = ADDRESS=15N HANCOCK ST, MADISON WI; PROJECT NAME=STUDY FOR A BACKLOT
  Height = 279.4
  Orientation = 1
  Width = 431.8
FEATURE [TechDraw::DrawViewSymbol] Symbol004
  EditableTexts = 01 | PLAN VIEW OF PARCEL - UNIFIED LOT | 1/32 = 1-0
  LockPosition = false
  Rotation = 0
  ScaleType = 2
  Symbol = <blob: 4979 chars omitted>
  X = 87.9124
  Y = 44.9176
FEATURE [TechDraw::DrawViewDraft] DraftView007
  Direction = (0,0,1)
  FontSize = 5.5
  LineSpacing = 5
  LineStyle = Solid
  LineWidth = 0.15
  LockPosition = false
  OverrideStyle = false
  Rotation = 0
  Scale = 0.00260417
  ScaleType = 2
  Source = -> Group001
  Symbol = <blob: 16881 chars omitted>
  X = -10.2463
  Y = 2.12375
FEATURE [TechDraw::DrawViewClip] Clip004
  Height = 213.36
  LockPosition = false
  Rotation = 0
  ScaleType = 0
  ShowFrame = false
  Views = -> [DraftView007]
  Width = 396.24
  X = 215.9
  Y = 155.7
FEATURE [TechDraw::DrawViewSymbol] Symbol005
  EditableTexts = OPTION 1 - PARKING SLOTS ONLY
  LockPosition = false
  Rotation = 0
  Scale = 2.1
  ScaleType = 2
  Symbol = <blob: 2122 chars omitted>
  X = 394.886
  Y = 11.6929
FEATURE [TechDraw::DrawPage] Page  label="Page 1 - parking only"
  KeepUpdated = true
  NextBalloonIndex = 1
  ProjectionType = 0
  Template = -> Template
  Views = -> [DraftView,Symbol,Symbol001,Clip001,DraftView001,Clip002,Symbol005]
FEATURE [TechDraw::DrawViewSymbol] Symbol006
  EditableTexts = OPTION 4 - SPLIT OT - OPEN-AIR PARKING
  LockPosition = false
  Rotation = 0
  Scale = 2.1
  ScaleType = 2
  Symbol = <blob: 2131 chars omitted>
  X = 396.011
  Y = 11.9197
FEATURE [TechDraw::DrawViewSymbol] Symbol007
  EditableTexts = OPTION 2 - SPLIT LOT
  LockPosition = false
  Rotation = 0
  Scale = 2.1
  ScaleType = 2
  Symbol = <blob: 2113 chars omitted>
  X = 395.161
  Y = 11.7296
FEATURE [TechDraw::DrawViewSymbol] Symbol008
  EditableTexts = OPTION 3 - UNIFIED LOT
  LockPosition = false
  Rotation = 0
  Scale = 2.1
  ScaleType = 2
  Symbol = <blob: 2115 chars omitted>
  X = 395.44
  Y = 11.8187
FEATURE [App::FeaturePython] Text020  # WARN: FeaturePython — macro-defined, semantics opaque (R4)
  Placement = pos=(8430.44,10871.8,0) rot=(0,0,-1;0.801487rad)
  Text = 660.32 SQFT
FEATURE [App::FeaturePython] Text021  # WARN: FeaturePython — macro-defined, semantics opaque (R4)
  Placement = pos=(6730.44,5771.84,0) rot=(0,0,-1;0.801487rad)
  Text = 988.22 SQFT
FEATURE [App::FeaturePython] Text022  # WARN: FeaturePython — macro-defined, semantics opaque (R4)
  Placement = pos=(6330.44,6271.84,0) rot=(0,0,-1;0.801487rad)
  Text = 98.22 SQFT
FEATURE [App::FeaturePython] Text023  # WARN: FeaturePython — macro-defined, semantics opaque (R4)
  Placement = pos=(8330.44,10871.8,0) rot=(0,0,-1;0.801487rad)
  Text = 660.32 SQFT
FEATURE [App::DocumentObjectGroup] Group003  label="Split lot without parking"
  Group = -> [Line051,Line052,Line047,Line046,Dimension018,Dimension016,Line050,Dimension017,Text015,Text016,Dimension019,Wire015,Text014,Dimension020,Dimension021,Text022,Text023]
FEATURE [TechDraw::DrawViewDraft] DraftView004
  Direction = (0,0,1)
  FontSize = 5.5
  LineSpacing = 3
  LineStyle = Solid
  LineWidth = 0.15
  LockPosition = false
  OverrideStyle = false
  Rotation = 0
  Scale = 0.00260417
  ScaleType = 2
  Source = -> Group003
  Symbol = <blob: 9737 chars omitted>
  X = 236.494
  Y = 187.752
FEATURE [TechDraw::DrawPage] Page002  label="Page 2 - split lot without parking"
  KeepUpdated = true
  NextBalloonIndex = 1
  ProjectionType = 0
  Template = -> Template002
  Views = -> [Symbol003,DraftView004,DraftView005,Clip003,Symbol007]
FEATURE [App::FeaturePython] Text024  # WARN: FeaturePython — macro-defined, semantics opaque (R4)
  Placement = pos=(10409.3,12806.3,0) rot=(0,0,-1;0.801487rad)
  Text = 2569.35 SQFT
FEATURE [Part::Part2DObjectPython] Wire017  label="Open space"  # Draft 2D object (typed FeaturePython)
  Area = 2.387e+08
  ChamferSize = 0
  Closed = true
  End = (17296.7,-6633.47,0)
  FilletRadius = 0
  Length = 84159.6
  MakeFace = true
  Placement = pos=(802.63,10577.6,0) rot=(0,0,1;0rad)
  Points = (8) [(0,0,0),(2792.49,2704.05,0),(5174.7,235.396,0),(15531.3,10224.8,0),(22540.4,2911,0),(12215.5,-7073.69,0),(19267.4,-14553.2,0),(16494,-17211.1,0)]
  Start = (802.63,10577.6,0)
  Subdivisions = 0
FEATURE [App::DocumentObjectGroup] Group004  label="Unified lot"
  Group = -> [Line054,Line055,Dimension022,Dimension025,Text017,Line057,Dimension028,Wire016,Text019,Dimension026,Dimension027,Wire017,Text024]
FEATURE [TechDraw::DrawViewDraft] DraftView006
  Direction = (0,0,1)
  FontSize = 5.5
  LineSpacing = 3
  LineStyle = Solid
  LineWidth = 0.15
  LockPosition = false
  OverrideStyle = false
  Rotation = 0
  Scale = 0.00260417
  ScaleType = 2
  Source = -> Group004
  Symbol = <blob: 7004 chars omitted>
  X = 247.81
  Y = 185.89
FEATURE [TechDraw::DrawPage] Page003  label="Page 3 - unified lot"
  KeepUpdated = true
  NextBalloonIndex = 1
  ProjectionType = 0
  Template = -> Template003
  Views = -> [Symbol004,DraftView006,DraftView007,Clip004,Symbol008]
FEATURE [Part::Part2DObjectPython] Line059  # Draft 2D object (typed FeaturePython)
  Area = 0
  ChamferSize = 0
  Closed = false
  End = (34256.7,26162.9,0)
  FilletRadius = 0
  Length = 4572.01
  MakeFace = true
  Points = (2) [(30970.2,22984.6,0),(34256.7,26162.9,0)]
  Start = (30970.2,22984.6,0)
  Subdivisions = 0
FEATURE [Part::Part2DObjectPython] Line060  # Draft 2D object (typed FeaturePython)
  Area = 0
  ChamferSize = 0
  Closed = false
  End = (31447.1,29068.2,0)
  FilletRadius = 0
  Length = 4572.01
  MakeFace = true
  Points = (2) [(28160.5,25889.9,0),(31447.1,29068.2,0)]
  Start = (28160.5,25889.9,0)
  Subdivisions = 0
FEATURE [App::FeaturePython] Dimension029  # Draft dimension (typed FeaturePython)
  Diameter = false
  Dimline = (35600,28800,0)
  Direction = (0,0,0)
  Distance = 4041.65
  End = (34256.7,26162.9,0)
  Normal = (0,0,1)
  Start = (31447.1,29068.2,0)
FEATURE [App::DocumentObjectGroup] Group  label="Split lot with parking"
  Group = -> [Line029,Line032,Line033,Line036,Dimension010,Dimension011,Line037,Dimension012,Text010,Text011,Dimension013,Line038,Line042,Line043,Line044,Line045,Wire014,Text012,Dimension014,Dimension015,Text013,Text020,Text021,Line059,Line060,Dimension029]
FEATURE [TechDraw::DrawViewDraft] DraftView009
  Direction = (0,0,1)
  FontSize = 5.5
  LineSpacing = 3
  LineStyle = Solid
  LineWidth = 0.15
  LockPosition = false
  OverrideStyle = false
  Rotation = 0
  Scale = 0.00260417
  ScaleType = 2
  Source = -> Group
  Symbol = <blob: 13640 chars omitted>
  X = 250.097
  Y = 184.079
FEATURE [TechDraw::DrawPage] Page001  label="Page 4 - split lot with parking"
  KeepUpdated = true
  NextBalloonIndex = 1
  ProjectionType = 0
  Template = -> Template001
  Views = -> [Symbol002,DraftView003,Clip,Symbol006,DraftView009]
